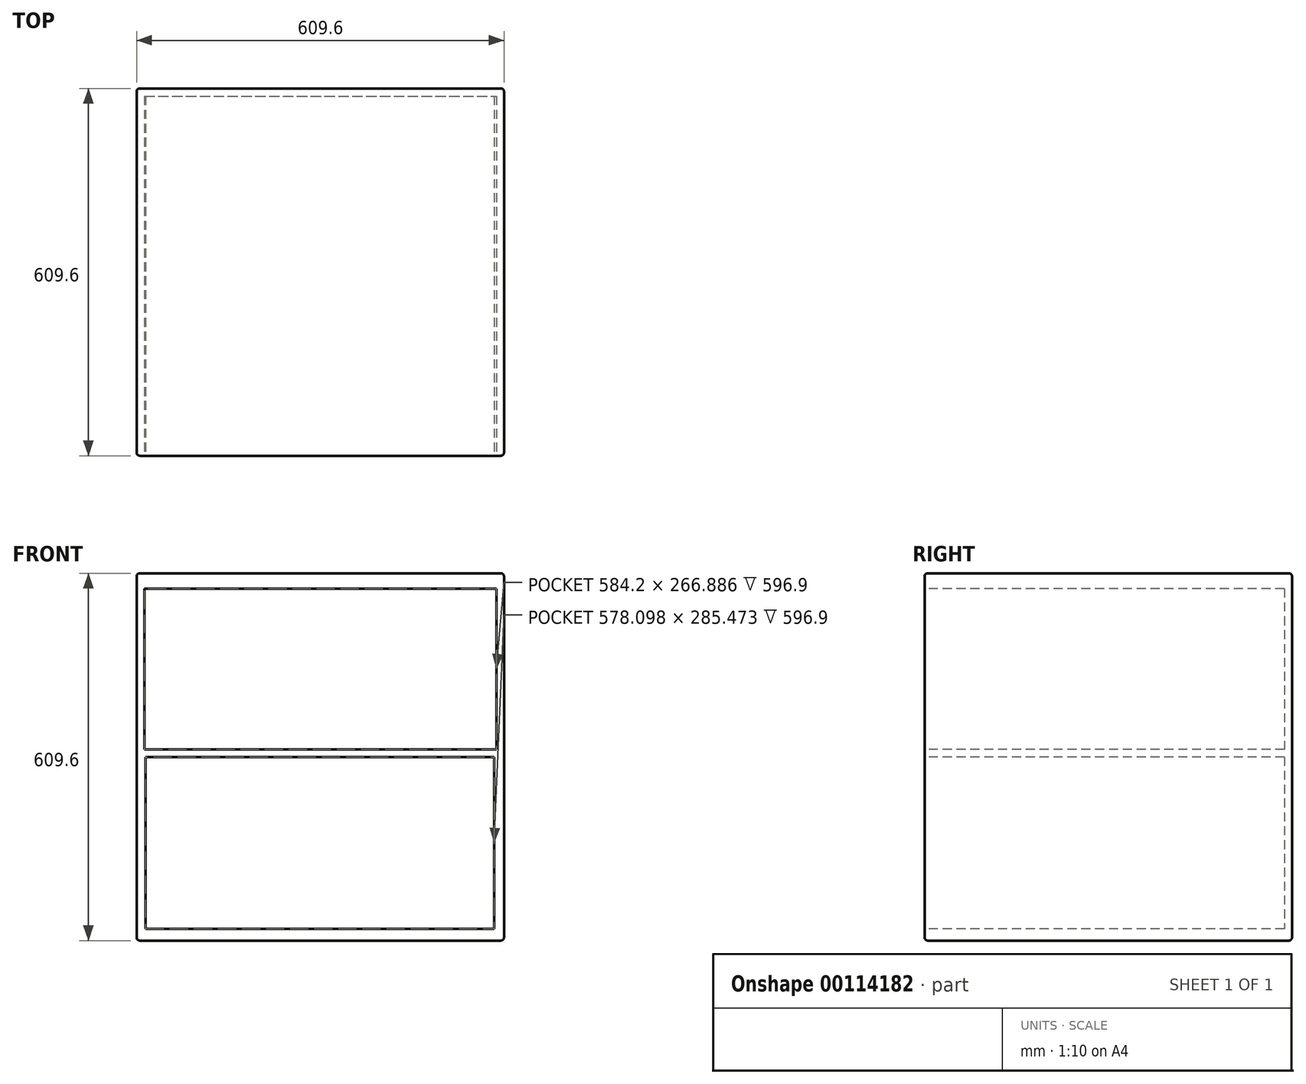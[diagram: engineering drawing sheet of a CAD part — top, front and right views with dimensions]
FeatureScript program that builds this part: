
annotation { "Feature Type Name" : "Feature", "Feature Type Description" : "" }
export const myFeature = defineFeature(function(context is Context, id is Id, definition is map)
    precondition{}
    {
        {
            var Q0;
            Q0=qCreatedBy(makeId("Front.planeOp"),FACE);
            var sketch = newSketch(context, id + "F0", { "sketchPlane" : qUnion([Q0])});
            skLineSegment(sketch, "E0.bottom", {"start": v(-304.8, 304.8) * mm, "end": v(304.8, 304.8) * mm});
            skLineSegment(sketch, "E0.top", {"start": v(-304.8, -304.8) * mm, "end": v(304.8, -304.8) * mm});
            skLineSegment(sketch, "E0.left", {"start": v(-304.8, 304.8) * mm, "end": v(-304.8, -304.8) * mm});
            skLineSegment(sketch, "E0.right", {"start": v(304.8, 304.8) * mm, "end": v(304.8, -304.8) * mm});
            skPoint(sketch, "E0.middle", {"position": v(0, 0) * mm});
            skSolve(sketch);
        }
        {
            var Q0;
            Q0=makeQuery(id+"F0.imprint","IMPRINT",FACE,{"disambiguationData":[TD([[makeQuery(id+"F0.imprint","IMPRINT",EDGE,{"derivedFrom":sQuery(id+"F0.wireOp",EDGE,"E0.bottom")}),-1.0]])]});
            extrude(context, id + "F1", {"entities" : qUnion([Q0]), "depth" : 609.6 * mm});
        }
        {
            var Q0;
            Q0=makeQuery(id+"F1.opExtrude","CAP_FACE",FACE,{"disambiguationData":[OSD([sQuery(id+"F0.wireOp",EDGE,"E0.bottom"),sQuery(id+"F0.wireOp",EDGE,"E0.top"),sQuery(id+"F0.wireOp",EDGE,"E0.left"),sQuery(id+"F0.wireOp",EDGE,"E0.right")])],"isStart":false});
            var sketch = newSketch(context, id + "F2", { "sketchPlane" : qUnion([Q0])});
            skLineSegment(sketch, "E1.bottom", {"start": v(-292.1, 279.4) * mm, "end": v(292.1, 279.4) * mm});
            skLineSegment(sketch, "E1.top", {"start": v(-292.1, -279.4) * mm, "end": v(292.1, -279.4) * mm});
            skLineSegment(sketch, "E1.left", {"start": v(-292.1, 279.4) * mm, "end": v(-292.1, -279.4) * mm});
            skLineSegment(sketch, "E1.right", {"start": v(292.1, 279.4) * mm, "end": v(292.1, -279.4) * mm});
            skPoint(sketch, "E1.middle", {"position": v(0, 0) * mm});
            skLineSegment(sketch, "E2.bottom", {"start": v(-292.1, 12.51) * mm, "end": v(292.1, 12.51) * mm});
            skLineSegment(sketch, "E2.top", {"start": v(-292.1, -12.51) * mm, "end": v(292.1, -12.51) * mm});
            skLineSegment(sketch, "E2.left", {"start": v(-292.1, 12.51) * mm, "end": v(-292.1, -12.51) * mm});
            skLineSegment(sketch, "E2.right", {"start": v(292.1, 12.51) * mm, "end": v(292.1, -12.51) * mm});
            skSolve(sketch);
        }
        {
            var Q0;
            Q0=makeQuery(id+"F1.opExtrude","CAP_EDGE",EDGE,{"disambiguationData":[OSD([sQuery(id+"F0.wireOp",EDGE,"E0.bottom")])],"isStart":false});
            fillet(context, id + "F3", {"entities" : qUnion([Q0]), "radius" : 5.08 * mm, "tangentPropagation" : true, "allowEdgeOverflow" : false});
        }
        {
            var Q0;
            Q0=makeQuery(id+"F1.opExtrude","CAP_EDGE",EDGE,{"disambiguationData":[OSD([sQuery(id+"F0.wireOp",EDGE,"E0.left")])],"isStart":false});
            var Q1;
            Q1=makeQuery(id+"F1.opExtrude","CAP_EDGE",EDGE,{"disambiguationData":[OSD([sQuery(id+"F0.wireOp",EDGE,"E0.right")])],"isStart":false});
            var Q2;
            Q2=makeQuery(id+"F1.opExtrude","CAP_EDGE",EDGE,{"disambiguationData":[OSD([sQuery(id+"F0.wireOp",EDGE,"E0.top")])],"isStart":false});
            fillet(context, id + "F4", {"entities" : qUnion([Q0, Q1, Q2]), "radius" : 5.08 * mm, "tangentPropagation" : true, "allowEdgeOverflow" : false});
        }
        {
            var Q0;
            Q0=makeQuery(id+"F1.opExtrude","SWEPT_EDGE",EDGE,{"disambiguationData":[OSD([sQuery(id+"F0.wireOp",EDGE,"E0.top"),sQuery(id+"F0.wireOp",EDGE,"E0.right")])]});
            var Q1;
            Q1=makeQuery(id+"F1.opExtrude","CAP_EDGE",EDGE,{"disambiguationData":[OSD([sQuery(id+"F0.wireOp",EDGE,"E0.right")])],"isStart":true});
            var Q2;
            Q2=makeQuery(id+"F1.opExtrude","CAP_EDGE",EDGE,{"disambiguationData":[OSD([sQuery(id+"F0.wireOp",EDGE,"E0.bottom")])],"isStart":true});
            var Q3;
            Q3=makeQuery(id+"F1.opExtrude","CAP_EDGE",EDGE,{"disambiguationData":[OSD([sQuery(id+"F0.wireOp",EDGE,"E0.left")])],"isStart":true});
            var Q4;
            Q4=makeQuery(id+"F1.opExtrude","CAP_EDGE",EDGE,{"disambiguationData":[OSD([sQuery(id+"F0.wireOp",EDGE,"E0.top")])],"isStart":true});
            var Q5;
            Q5=makeQuery(id+"F1.opExtrude","SWEPT_EDGE",EDGE,{"disambiguationData":[OSD([sQuery(id+"F0.wireOp",EDGE,"E0.top"),sQuery(id+"F0.wireOp",EDGE,"E0.left")])]});
            var Q6;
            {var subQ0=sQuery(id+"F0.wireOp",EDGE,"E0.right");Q6=makeQuery(id+"F4.opFillet","BLEND_EDGE",EDGE,{"blendedFrom":[makeQuery(id+"F1.opExtrude","SWEPT_EDGE",EDGE,{"disambiguationData":[OSD([sQuery(id+"F0.wireOp",EDGE,"E0.bottom"),subQ0])]}),makeQuery(id+"F1.opExtrude","SWEPT_FACE",FACE,{"disambiguationData":[OSD([subQ0])]})],"blendedInto":[makeQuery(id+"F1.opExtrude","SWEPT_FACE",FACE,{"disambiguationData":[OSD([subQ0])]})]});}
            fillet(context, id + "F5", {"entities" : qUnion([Q0, Q1, Q2, Q3, Q4, Q5, Q6]), "radius" : 5.08 * mm, "tangentPropagation" : true, "allowEdgeOverflow" : false});
        }
        {
            var Q0;
            {var subQ0=sQuery(id+"F2.wireOp",EDGE,"E1.bottom");Q0=makeQuery(id+"F2.imprint","IMPRINT",FACE,{"disambiguationData":[TD([[makeQuery(id+"F2.imprint","IMPRINT",EDGE,{"derivedFrom":subQ0}),-1.0]])]});}
            extrude(context, id + "F6", {"entities" : qUnion([Q0]), "operationType" : NewBodyOperationType.REMOVE, "oppositeDirection" : true, "depth" : 596.9 * mm});
        }
        {
            var Q0;
            Q0=makeQuery(id+"F1.opExtrude","CAP_FACE",FACE,{"disambiguationData":[OSD([sQuery(id+"F0.wireOp",EDGE,"E0.bottom"),sQuery(id+"F0.wireOp",EDGE,"E0.top"),sQuery(id+"F0.wireOp",EDGE,"E0.left"),sQuery(id+"F0.wireOp",EDGE,"E0.right")])],"isStart":false});
            var sketch = newSketch(context, id + "F7", { "sketchPlane" : qUnion([Q0])});
            skPoint(sketch, "E3.firstSnap0", {"position": v(-299.72, 0) * mm});
            skLineSegment(sketch, "E3.bottom", {"start": v(-289.65, 0) * mm, "end": v(288.45, 0) * mm});
            skLineSegment(sketch, "E3.top", {"start": v(-289.65, -285.47) * mm, "end": v(288.45, -285.47) * mm});
            skLineSegment(sketch, "E3.left", {"start": v(-289.65, 0) * mm, "end": v(-289.65, -285.47) * mm});
            skLineSegment(sketch, "E3.right", {"start": v(288.45, 0) * mm, "end": v(288.45, -285.47) * mm});
            skSolve(sketch);
        }
        {
            var Q0;
            Q0=makeQuery(id+"F7.imprint","IMPRINT",FACE,{"disambiguationData":[TD([[makeQuery(id+"F7.imprint","IMPRINT",EDGE,{"derivedFrom":sQuery(id+"F7.wireOp",EDGE,"E3.bottom")}),-1.0]])]});
            extrude(context, id + "F8", {"entities" : qUnion([Q0]), "operationType" : NewBodyOperationType.REMOVE, "oppositeDirection" : true, "depth" : 596.9 * mm});
        }
    });
